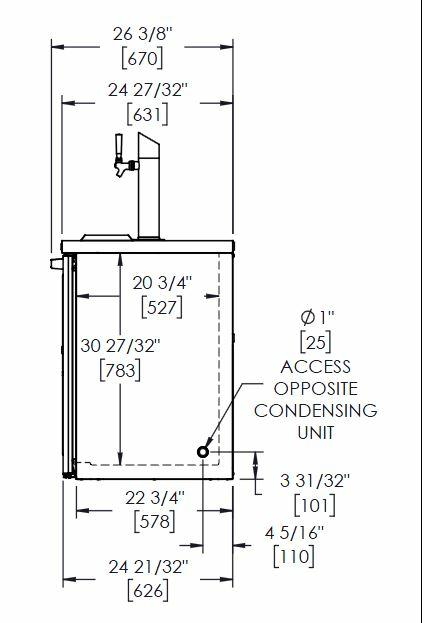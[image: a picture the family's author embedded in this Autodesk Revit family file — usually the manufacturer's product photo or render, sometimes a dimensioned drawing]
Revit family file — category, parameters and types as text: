
# Revit family: QF_TRUE_TDR48-RISZ1-L-B-SS-1
name_source: partatom
category: Specialty Equipment
revit_build: Autodesk Revit 2016 (Build: 20150714_1515(x64)
units: mm (PartAtom-declared; Revit-internal decimal feet)

## family parameters
Always vertical = Yes
Cut with Voids When Loaded = No
Part Type = Normal
Room Calculation Point = No
Round Connector Dimension = Use Diameter
Shared = No
Work Plane-Based = No

## types (1)
- QF_TRUE_TDR48-RISZ1-L-B-SS-1
    Apparent Power = 207 VA
    Condensate Return Connection Height = 0"
    Condensate Return RI Height = 0"
    Condensate Return Size = 1"
    Conn Conduit = Yes
    Conn Plug = NEMA 5-15P
    Cycle = 60 Hz
    Depth = 26 3/8"
    Description = REACH-IN SINGLE ZONE REFRIGERATOR WITH LEFT SIDE REFRIGERATION SYSTEM. BLACK EXTERIOR AND SOLID SWING DOORS
    Elec Conn Connection Height = 0"
    Elec Conn RI Height = 0"
    FL Amps = 2 A
    Foodservice Equipment Identifier = Yes
    HP = 1/4
    Identify Quantity as Lot = Yes
    Indirect Waste Connection Height = 0"
    Indirect Waste Flow = 0 GPM
    Indirect Waste Size = 1"
    Length = 48"
    Manufacturer = TRUE
    Max Overcurrent Protection = 0 A
    Min Ckt Ampacity = 0 A
    Model = TDR48-RISZ1-L-B-SS-1
    Number of Poles = 1
    Phase = 1
    Steam Supply Connection Height = 0"
    Steam Supply Maximum Pressure = 0.00 psi
    Steam Supply Minimum Pressure = 0.00 psi
    Steam Supply RI Height = 0"
    Steam Supply Size = 0"
    Steam Supply Volume = 0 GPM
    Volts = 115 V
    Waste Water Discharge Temperature = 0 °F
    Watts = 207 W
    Weight in Pounds = 405

## geometry (parser evidence)
native form markers: Sweep x23
no freeform markers — native parametric forms only
